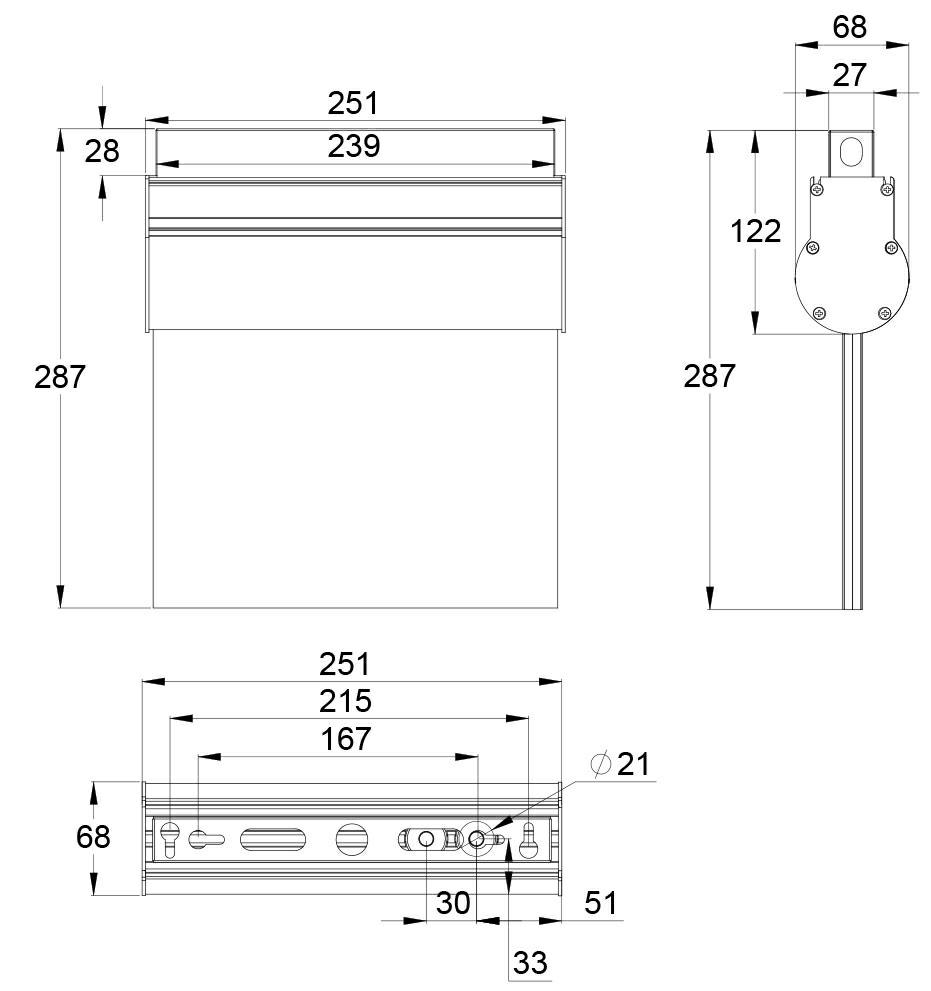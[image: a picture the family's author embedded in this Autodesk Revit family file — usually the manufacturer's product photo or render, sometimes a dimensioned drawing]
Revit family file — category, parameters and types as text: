
# Revit family: ESC 10 LED EMERGENCY EXIT LIGHT TW85051WK
name_source: partatom
category: Electrical Fixtures
revit_build: Autodesk Revit 2015 (Build: 20160512_0715(x64)
units: mm (PartAtom-declared; Revit-internal decimal feet)

## types (3) — shared parameters
Depth = 68 mm
Height = 259 mm  [stored 0.849738 ft]
Manufacturer = Teknoware Oy
Model = ESC 10 TW850
Product Code = TW85051WK
Viewing Distance = 30000 mm  [stored 98.4252 ft]
Width = 251 mm  [stored 0.823491 ft]

## per-type parameters (varying)
| type | Back Pictogram | Down | Front Pictogram | Left | Right | Type Comments |
| -arrow right | Teknoware Pictogram PBV10301E left | No | Teknoware Pictogram PBV10301E right | No | Yes | PBV10301E |
| -arrow left | Teknoware Pictogram PBV10301E right | No | Teknoware Pictogram PBV10301E left | Yes | No | PBV10301E |
| -arrow down | Teknoware Pictogram PBV10302E | Yes | Teknoware Pictogram PBV10302E | No | No | PBV10302E |

note: [stored X ft] marks values corroborated as IEEE doubles in the binary element streams (Revit-internal decimal feet)

## geometry (parser evidence)
native form markers: Blend x6, Sweep x11
no freeform markers — native parametric forms only
